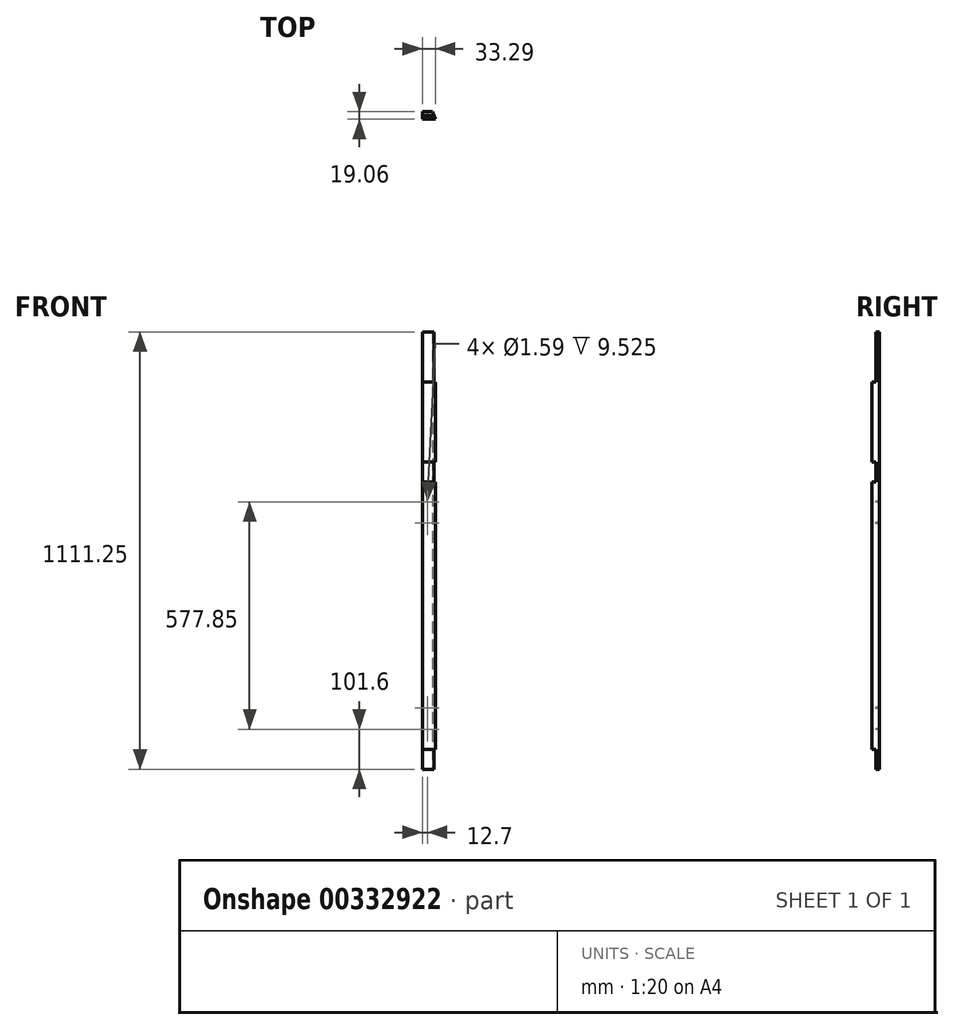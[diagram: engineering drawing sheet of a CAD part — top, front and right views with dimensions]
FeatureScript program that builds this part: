
annotation { "Feature Type Name" : "Feature", "Feature Type Description" : "" }
export const myFeature = defineFeature(function(context is Context, id is Id, definition is map)
    precondition{}
    {
        {
            var Q0;
            Q0=qCreatedBy(makeId("Top.planeOp"),FACE);
            var sketch = newSketch(context, id + "F0", { "sketchPlane" : qUnion([Q0])});
            skLineSegment(sketch, "E0.bottom", {"start": v(0, 9.53) * mm, "end": v(-25.4, 9.53) * mm});
            skLineSegment(sketch, "E0.top", {"start": v(7.9, -9.53) * mm, "end": v(-25.4, -9.53) * mm});
            skLineSegment(sketch, "E0.right", {"start": v(-25.4, 9.53) * mm, "end": v(-25.4, -9.53) * mm});
            skPoint(sketch, "E0.middle", {"position": v(0, 0) * mm});
            skLineSegment(sketch, "E1", {"start": v(0, 9.53) * mm, "end": v(7.9, -9.53) * mm});
            skPoint(sketch, "E0.left.end.orphan", {"position": v(25.4, -9.52) * mm});
            skPoint(sketch, "E2.orphan", {"position": v(25.4, 9.53) * mm});
            skSolve(sketch);
        }
        {
            var Q0;
            Q0=makeQuery(id+"F0.imprint","IMPRINT",FACE,{"disambiguationData":[TD([[makeQuery(id+"F0.imprint","IMPRINT",EDGE,{"derivedFrom":sQuery(id+"F0.wireOp",EDGE,"E0.bottom")}),1.0]])]});
            extrude(context, id + "F1", {"entities" : qUnion([Q0]), "depth" : 1111.25 * mm});
        }
        {
            var Q0;
            Q0=qCreatedBy(makeId("Front.planeOp"),FACE);
            var sketch = newSketch(context, id + "F2", { "sketchPlane" : qUnion([Q0])});
            skLineSegment(sketch, "E3.bottom", {"start": v(-38.77, 0) * mm, "end": v(83.66, 0) * mm});
            skLineSegment(sketch, "E3.top", {"start": v(-38.77, 50.8) * mm, "end": v(83.66, 50.8) * mm});
            skLineSegment(sketch, "E3.left", {"start": v(-38.77, 0) * mm, "end": v(-38.77, 50.8) * mm});
            skLineSegment(sketch, "E3.right", {"start": v(83.66, 0) * mm, "end": v(83.66, 50.8) * mm});
            skLineSegment(sketch, "E4.bottom", {"start": v(-44.21, 730.25) * mm, "end": v(49.65, 730.25) * mm});
            skLineSegment(sketch, "E4.top", {"start": v(-44.21, 781.05) * mm, "end": v(49.65, 781.05) * mm});
            skLineSegment(sketch, "E4.left", {"start": v(-44.21, 730.25) * mm, "end": v(-44.21, 781.05) * mm});
            skLineSegment(sketch, "E4.right", {"start": v(49.65, 730.25) * mm, "end": v(49.65, 781.05) * mm});
            skLineSegment(sketch, "E5.bottom", {"start": v(-210.36, 984.25) * mm, "end": v(132.8, 984.25) * mm});
            skLineSegment(sketch, "E5.top", {"start": v(-210.36, 1111.25) * mm, "end": v(132.8, 1111.25) * mm});
            skLineSegment(sketch, "E5.left", {"start": v(-210.36, 984.25) * mm, "end": v(-210.36, 1111.25) * mm});
            skLineSegment(sketch, "E5.right", {"start": v(132.8, 984.25) * mm, "end": v(132.8, 1111.25) * mm});
            skSolve(sketch);
        }
        {
            var Q0;
            Q0=qSketchRegion(id+"F2",true);
            extrude(context, id + "F3", {"entities" : qUnion([Q0]), "operationType" : NewBodyOperationType.REMOVE, "depth" : 25.4 * mm});
        }
        {
            var Q0;
            Q0=qCreatedBy(makeId("Front.planeOp"),FACE);
            var sketch = newSketch(context, id + "F4", { "sketchPlane" : qUnion([Q0])});
            skCircle(sketch, "E6", {"center": v(12.7, 101.6) * mm, "radius": 0.8 * mm});
            skCircle(sketch, "E7", {"center": v(12.7, 155.58) * mm, "radius": 0.8 * mm});
            skCircle(sketch, "E8", {"center": v(12.7, 625.48) * mm, "radius": 0.8 * mm});
            skCircle(sketch, "E9", {"center": v(12.7, 679.45) * mm, "radius": 0.8 * mm});
            skLineSegment(sketch, "E10", {"start": v(0, 0) * mm, "end": v(0, 1192.46) * mm, "construction": true});
            skLineSegment(sketch, "E11.bottom", {"start": v(12.7, 101.6) * mm, "end": v(-12.7, 101.6) * mm, "construction": true});
            skLineSegment(sketch, "E11.top", {"start": v(12.7, 679.45) * mm, "end": v(-12.7, 679.45) * mm, "construction": true});
            skLineSegment(sketch, "E11.left", {"start": v(12.7, 101.6) * mm, "end": v(12.7, 679.45) * mm, "construction": true});
            skLineSegment(sketch, "E11.right", {"start": v(-12.7, 101.6) * mm, "end": v(-12.7, 679.45) * mm, "construction": true});
            skCircle(sketch, "E12", {"center": v(-12.7, 625.48) * mm, "radius": 0.8 * mm});
            skCircle(sketch, "E13", {"center": v(-12.7, 679.45) * mm, "radius": 0.8 * mm});
            skCircle(sketch, "E14", {"center": v(-12.7, 101.6) * mm, "radius": 0.8 * mm});
            skCircle(sketch, "E15", {"center": v(-12.7, 155.58) * mm, "radius": 0.8 * mm});
            skSolve(sketch);
        }
        {
            var Q0;
            Q0=qSketchRegion(id+"F4",true);
            extrude(context, id + "F5", {"entities" : qUnion([Q0]), "operationType" : NewBodyOperationType.REMOVE, "oppositeDirection" : true, "depth" : 25.4 * mm});
        }
    });
